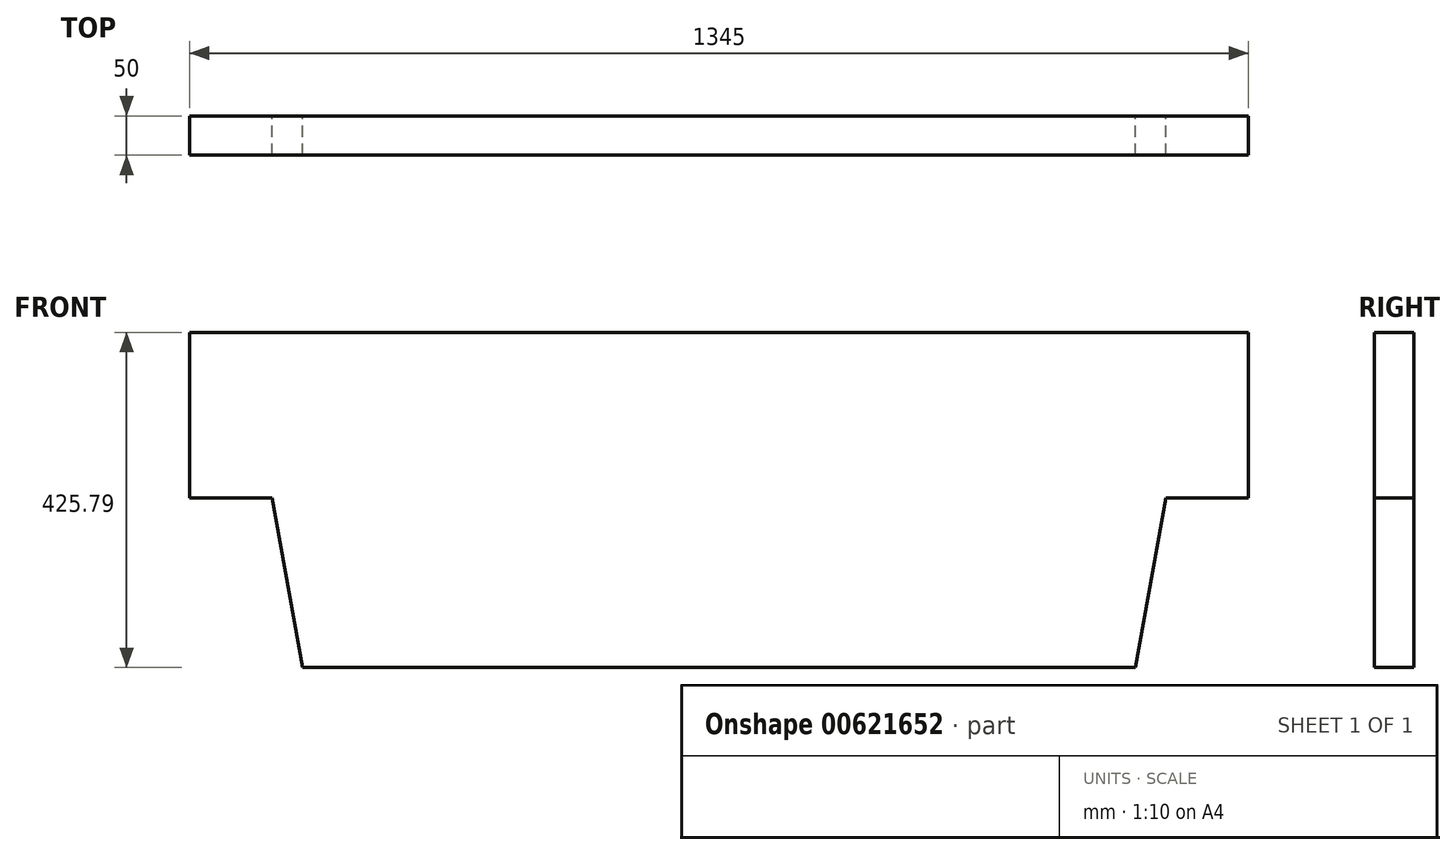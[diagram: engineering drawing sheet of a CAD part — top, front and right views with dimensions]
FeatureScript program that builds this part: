
annotation { "Feature Type Name" : "Feature", "Feature Type Description" : "" }
export const myFeature = defineFeature(function(context is Context, id is Id, definition is map)
    precondition{}
    {
        {
            var Q0;
            Q0=qCreatedBy(makeId("Top.planeOp"),FACE);
            var sketch = newSketch(context, id + "F0", { "sketchPlane" : qUnion([Q0])});
            skLineSegment(sketch, "E0.bottom", {"start": v(0, 0) * mm, "end": v(520, 0) * mm});
            skLineSegment(sketch, "E0.top", {"start": v(0, 510) * mm, "end": v(520, 510) * mm});
            skLineSegment(sketch, "E0.left", {"start": v(0, 0) * mm, "end": v(0, 510) * mm});
            skLineSegment(sketch, "E0.right", {"start": v(520, 0) * mm, "end": v(520, 510) * mm});
            skSolve(sketch);
        }
        {
            var Q0;
            Q0=sQuery(id+"F0.wireOp",EDGE,"E0.left");
            cPoint(context, id + "F1", {"entities" : qUnion([Q0]), "parameter" : 0.5});
        }
        {
            var Q0;
            Q0=qCreatedBy(makeId("Front.planeOp"),FACE);
            var Q1;
            Q1 = qCreatedBy(id + "F1" ,VERTEX);
            cPlane(context, id + "F2", {"entities" : qUnion([Q0, Q1]), "cplaneType" : CPlaneType.PLANE_POINT, "offset" : 25 * mm, "width" : 150 * mm, "height" : 150 * mm});
        }
        {
            var Q0;
            Q0=qCreatedBy(id+"F2.planeOp",FACE);
            var sketch = newSketch(context, id + "F3", { "sketchPlane" : qUnion([Q0])});
            skLineSegment(sketch, "E1", {"start": v(0, 0) * mm, "end": v(-8.94, 50) * mm, "construction": true});
            skLineSegment(sketch, "E2", {"start": v(-47.5, 265.79) * mm, "end": v(-152.5, 265.79) * mm});
            skLineSegment(sketch, "E3", {"start": v(-152.5, 265.79) * mm, "end": v(-152.5, 475.79) * mm});
            skLineSegment(sketch, "E4", {"start": v(-152.5, 475.79) * mm, "end": v(1192.5, 475.79) * mm});
            skLineSegment(sketch, "E5", {"start": v(1192.5, 475.79) * mm, "end": v(1192.5, 265.79) * mm});
            skLineSegment(sketch, "E6", {"start": v(1192.5, 265.79) * mm, "end": v(1087.5, 265.79) * mm});
            skLineSegment(sketch, "E7", {"start": v(1087.5, 265.79) * mm, "end": v(1048.94, 50) * mm});
            skLineSegment(sketch, "E8", {"start": v(1040, 0) * mm, "end": v(0, 0) * mm, "construction": true});
            skLineSegment(sketch, "E9", {"start": v(520, 0) * mm, "end": v(520, 475.79) * mm, "construction": true});
            skLineSegment(sketch, "E10", {"start": v(-8.94, 50) * mm, "end": v(1048.94, 50) * mm});
            skLineSegment(sketch, "E11", {"start": v(-8.94, 50) * mm, "end": v(-47.5, 265.79) * mm});
            skLineSegment(sketch, "E12", {"start": v(1048.94, 50) * mm, "end": v(1040, 0) * mm, "construction": true});
            skSolve(sketch);
        }
        {
            var Q0;
            Q0 = qSketchRegion(id + "F3", true);
            var Q1;
            Q1=sQuery(id+"F0.wireOp",VERTEX,"E0.right.start");
            var Q2;
            Q2=sQuery(id+"F0.wireOp",VERTEX,"E0.right.end");
            extrude(context, id + "F4", {"entities" : qUnion([Q0]), "depth" : 50 * mm, "endBoundEntityVertex" : qUnion([Q1]), "offsetDistance" : 25 * mm});
        }
    });
